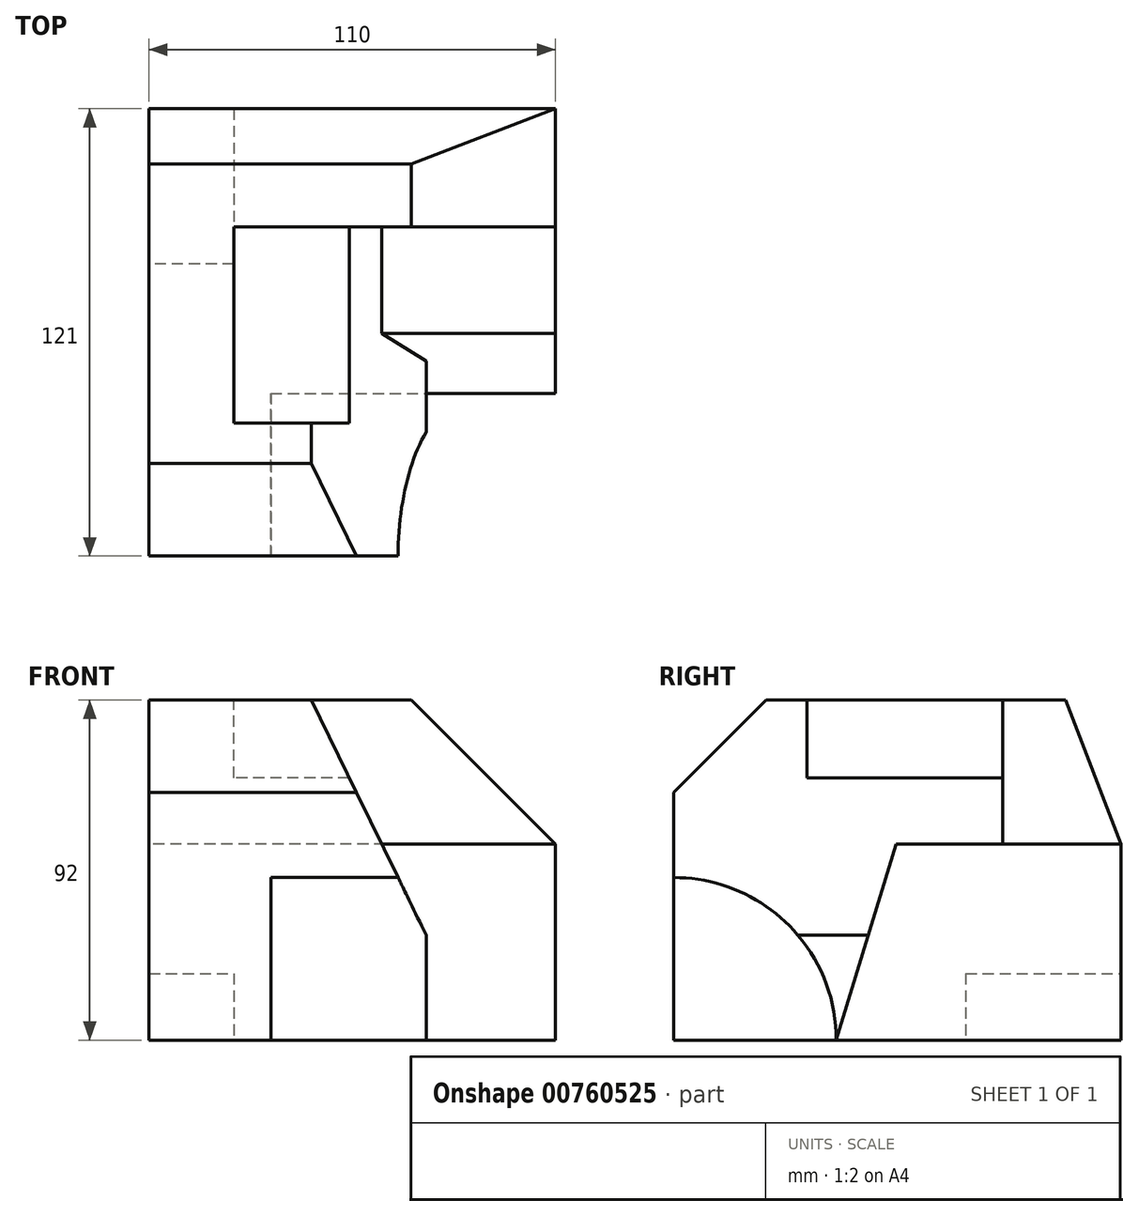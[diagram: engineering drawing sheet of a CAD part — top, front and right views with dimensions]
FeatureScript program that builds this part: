
annotation { "Feature Type Name" : "Feature", "Feature Type Description" : "" }
export const myFeature = defineFeature(function(context is Context, id is Id, definition is map)
    precondition{}
    {
        {
            var Q0;
            Q0=qCreatedBy(makeId("Front.planeOp"),FACE);
            var sketch = newSketch(context, id + "F0", { "sketchPlane" : qUnion([Q0])});
            skLineSegment(sketch, "E0", {"start": v(0, 0) * mm, "end": v(0, 92) * mm});
            skLineSegment(sketch, "E1", {"start": v(0, 92) * mm, "end": v(44, 92) * mm});
            skLineSegment(sketch, "E2", {"start": v(44, 92) * mm, "end": v(75, 28.44) * mm});
            skLineSegment(sketch, "E3", {"start": v(75, 28.44) * mm, "end": v(75, 0) * mm});
            skLineSegment(sketch, "E4", {"start": v(75, 0) * mm, "end": v(0, 0) * mm});
            skLineSegment(sketch, "E5", {"start": v(44, 92) * mm, "end": v(113.49, 92) * mm});
            skLineSegment(sketch, "E6", {"start": v(113.49, 92) * mm, "end": v(113.49, 53) * mm});
            skLineSegment(sketch, "E7", {"start": v(113.49, 53) * mm, "end": v(63.02, 53) * mm});
            skSolve(sketch);
        }
        {
            var Q0;
            Q0=qCreatedBy(makeId("Top.planeOp"),FACE);
            var sketch = newSketch(context, id + "F1", { "sketchPlane" : qUnion([Q0])});
            skLineSegment(sketch, "E8", {"start": v(0, 0) * mm, "end": v(0, 121) * mm});
            skLineSegment(sketch, "E9", {"start": v(0, 121) * mm, "end": v(110, 121) * mm});
            skLineSegment(sketch, "E10", {"start": v(110, 121) * mm, "end": v(110, 0) * mm});
            skLineSegment(sketch, "E11", {"start": v(110, 0) * mm, "end": v(0, 0) * mm});
            skLineSegment(sketch, "E12", {"start": v(0, 121) * mm, "end": v(23, 121) * mm});
            skLineSegment(sketch, "E13", {"start": v(23, 121) * mm, "end": v(23, 79) * mm});
            skLineSegment(sketch, "E14", {"start": v(23, 79) * mm, "end": v(0, 79) * mm});
            skLineSegment(sketch, "E15", {"start": v(0, 79) * mm, "end": v(0, 121) * mm});
            skSolve(sketch);
        }
        {
            var Q0;
            Q0=qCreatedBy(makeId("Right.planeOp"),FACE);
            var sketch = newSketch(context, id + "F2", { "sketchPlane" : qUnion([Q0])});
            skLineSegment(sketch, "E16", {"start": v(0, 0) * mm, "end": v(0, 67) * mm});
            skLineSegment(sketch, "E17", {"start": v(0, 67) * mm, "end": v(25, 92) * mm});
            skLineSegment(sketch, "E18", {"start": v(25, 92) * mm, "end": v(106.03, 92) * mm});
            skLineSegment(sketch, "E19", {"start": v(106.03, 92) * mm, "end": v(121, 53) * mm});
            skLineSegment(sketch, "E20", {"start": v(121, 53) * mm, "end": v(121, 0) * mm});
            skLineSegment(sketch, "E21", {"start": v(121, 0) * mm, "end": v(0, 0) * mm});
            skSolve(sketch);
        }
        {
            var Q0;
            Q0=makeQuery(id+"F0.imprint","IMPRINT",FACE,{"disambiguationData":[TD([[makeQuery(id+"F0.imprint","IMPRINT",EDGE,{"derivedFrom":sQuery(id+"F0.wireOp",EDGE,"E0")}),-1.0]])]});
            extrude(context, id + "F3", {"entities" : qUnion([Q0]), "oppositeDirection" : true, "depth" : 172 * mm, "offsetDistance" : 25 * mm});
        }
        {
            var Q0;
            Q0=makeQuery(id+"F2.imprint","IMPRINT",FACE,{"disambiguationData":[TD([[makeQuery(id+"F2.imprint","IMPRINT",EDGE,{"derivedFrom":sQuery(id+"F2.wireOp",EDGE,"E16")}),-1.0]])]});
            extrude(context, id + "F4", {"entities" : qUnion([Q0]), "operationType" : NewBodyOperationType.INTERSECT, "depth" : 150 * mm, "offsetDistance" : 25 * mm});
        }
        {
            var Q0;
            Q0=qCreatedBy(makeId("Front.planeOp"),FACE);
            cPlane(context, id + "F5", {"entities" : qUnion([Q0]), "cplaneType" : CPlaneType.OFFSET, "offset" : 44 * mm, "oppositeDirection" : true, "width" : 150 * mm, "height" : 150 * mm});
        }
        {
            var Q0;
            Q0=qCreatedBy(id+"F5.planeOp",FACE);
            var sketch = newSketch(context, id + "F6", { "sketchPlane" : qUnion([Q0])});
            skLineSegment(sketch, "E22", {"start": v(0, 0) * mm, "end": v(0, 92) * mm});
            skLineSegment(sketch, "E23", {"start": v(0, 92) * mm, "end": v(71, 92) * mm});
            skLineSegment(sketch, "E24", {"start": v(71, 92) * mm, "end": v(110, 53) * mm});
            skLineSegment(sketch, "E25", {"start": v(110, 53) * mm, "end": v(110, 0) * mm});
            skLineSegment(sketch, "E26", {"start": v(110, 0) * mm, "end": v(0, 0) * mm});
            skSolve(sketch);
        }
        {
            var Q0;
            Q0=makeQuery(id+"F6.imprint","IMPRINT",FACE,{"disambiguationData":[TD([[makeQuery(id+"F6.imprint","IMPRINT",EDGE,{"derivedFrom":sQuery(id+"F6.wireOp",EDGE,"E22")}),-1.0]])]});
            extrude(context, id + "F7", {"entities" : qUnion([Q0]), "oppositeDirection" : true, "depth" : 111 * mm, "offsetDistance" : 25 * mm});
        }
        {
            var Q0;
            Q0=makeQuery(id+"F2.imprint","IMPRINT",FACE,{"disambiguationData":[TD([[makeQuery(id+"F2.imprint","IMPRINT",EDGE,{"derivedFrom":sQuery(id+"F2.wireOp",EDGE,"E16")}),-1.0]])]});
            extrude(context, id + "F8", {"entities" : qUnion([Q0]), "operationType" : NewBodyOperationType.INTERSECT, "depth" : 163 * mm, "offsetDistance" : 25 * mm});
        }
        {
            var Q0;
            Q0=makeQuery(id+"F3.opExtrude","SWEPT_FACE",FACE,{"disambiguationData":[OSD([sQuery(id+"F0.wireOp",EDGE,"E3")])]});
            var sketch = newSketch(context, id + "F9", { "sketchPlane" : qUnion([Q0])});
            skCircle(sketch, "E27", {"center": v(0, 0) * mm, "radius": 44 * mm});
            skSolve(sketch);
        }
        {
            var Q0;
            {var subQ1=sQuery(id+"F0.wireOp",EDGE,"E3");var subQ6=makeQuery(id+"F3.opExtrude","CAP_EDGE",EDGE,{"disambiguationData":[OSD([subQ1])],"isStart":true});Q0=makeQuery(id+"F9.imprint","IMPRINT",FACE,{"disambiguationData":[TD([[makeQuery(id+"F9.imprint","IMPRINT",EDGE,{"derivedFrom":subQ6}),1.0]])]});}
            var Q1;
            {var subQ1=sQuery(id+"F0.wireOp",EDGE,"E3");var subQ6=makeQuery(id+"F3.opExtrude","CAP_EDGE",EDGE,{"disambiguationData":[OSD([subQ1])],"isStart":true});Q1=makeQuery(id+"F9.imprint","IMPRINT",FACE,{"disambiguationData":[TD([[makeQuery(id+"F9.imprint","IMPRINT",EDGE,{"derivedFrom":subQ6}),-1.0]])]});}
            extrude(context, id + "F10", {"entities" : qUnion([Q0, Q1]), "operationType" : NewBodyOperationType.REMOVE, "oppositeDirection" : true, "depth" : 42 * mm, "offsetDistance" : 25 * mm});
        }
        {
            var Q0;
            {var subQ0=sQuery(id+"F0.wireOp",EDGE,"E5");Q0=makeQuery(id+"F0.imprint","IMPRINT",FACE,{"disambiguationData":[TD([[makeQuery(id+"F0.imprint","IMPRINT",EDGE,{"derivedFrom":subQ0}),-1.0]])]});}
            extrude(context, id + "F11", {"entities" : qUnion([Q0]), "oppositeDirection" : true, "depth" : 89 * mm, "offsetDistance" : 25 * mm});
        }
        {
            var Q0;
            Q0=makeQuery(id+"F11.opExtrude","SWEPT_BODY",BODY,{"disambiguationData":[OSD([sQuery(id+"F0.wireOp",EDGE,"E2"),sQuery(id+"F0.wireOp",EDGE,"E5"),sQuery(id+"F0.wireOp",EDGE,"E6"),sQuery(id+"F0.wireOp",EDGE,"E7")])]});
            var Q1;
            Q1=makeQuery(id+"F7.opExtrude","SWEPT_BODY",BODY,{"disambiguationData":[OSD([sQuery(id+"F6.wireOp",EDGE,"E22"),sQuery(id+"F6.wireOp",EDGE,"E23"),sQuery(id+"F6.wireOp",EDGE,"E24"),sQuery(id+"F6.wireOp",EDGE,"E25"),sQuery(id+"F6.wireOp",EDGE,"E26")])]});
            booleanBodies(context, id + "F12", {"operationType" : BooleanOperationType.SUBTRACTION, "tools" : qUnion([Q0]), "targets" : qUnion([Q1])});
        }
        {
            var Q0;
            Q0=makeQuery(id+"F7.opExtrude","SWEPT_FACE",FACE,{"disambiguationData":[OSD([sQuery(id+"F6.wireOp",EDGE,"E25")])]});
            var sketch = newSketch(context, id + "F13", { "sketchPlane" : qUnion([Q0])});
            skLineSegment(sketch, "E28", {"start": v(44, 0) * mm, "end": v(60.2, 53) * mm});
            skLineSegment(sketch, "E29", {"start": v(60.2, 53) * mm, "end": v(44, 53) * mm});
            skLineSegment(sketch, "E30", {"start": v(44, 53) * mm, "end": v(44, 0) * mm});
            skSolve(sketch);
        }
        {
            var Q0;
            Q0=makeQuery(id+"F13.imprint","IMPRINT",FACE,{"disambiguationData":[TD([[makeQuery(id+"F13.imprint","IMPRINT",EDGE,{"derivedFrom":sQuery(id+"F13.wireOp",EDGE,"E28")}),1.0]])]});
            extrude(context, id + "F14", {"entities" : qUnion([Q0]), "oppositeDirection" : true, "depth" : 110 * mm, "offsetDistance" : 25 * mm});
        }
        {
            var Q0;
            Q0=makeQuery(id+"F14.opExtrude","SWEPT_BODY",BODY,{"disambiguationData":[OSD([sQuery(id+"F13.wireOp",EDGE,"E28"),sQuery(id+"F13.wireOp",EDGE,"E29"),sQuery(id+"F13.wireOp",EDGE,"E30")])]});
            var Q1;
            Q1=makeQuery(id+"F7.opExtrude","SWEPT_BODY",BODY,{"disambiguationData":[OSD([sQuery(id+"F6.wireOp",EDGE,"E22"),sQuery(id+"F6.wireOp",EDGE,"E23"),sQuery(id+"F6.wireOp",EDGE,"E24"),sQuery(id+"F6.wireOp",EDGE,"E25"),sQuery(id+"F6.wireOp",EDGE,"E26")])]});
            booleanBodies(context, id + "F15", {"operationType" : BooleanOperationType.SUBTRACTION, "tools" : qUnion([Q0]), "targets" : qUnion([Q1])});
        }
        {
            var Q0;
            Q0=makeQuery(id+"F3.opExtrude","SWEPT_BODY",BODY,{"disambiguationData":[OSD([sQuery(id+"F0.wireOp",EDGE,"E0"),sQuery(id+"F0.wireOp",EDGE,"E1"),sQuery(id+"F0.wireOp",EDGE,"E2"),sQuery(id+"F0.wireOp",EDGE,"E3"),sQuery(id+"F0.wireOp",EDGE,"E4")])]});
            var Q1;
            Q1=makeQuery(id+"F7.opExtrude","SWEPT_BODY",BODY,{"disambiguationData":[OSD([sQuery(id+"F6.wireOp",EDGE,"E22"),sQuery(id+"F6.wireOp",EDGE,"E23"),sQuery(id+"F6.wireOp",EDGE,"E24"),sQuery(id+"F6.wireOp",EDGE,"E25"),sQuery(id+"F6.wireOp",EDGE,"E26")])]});
            booleanBodies(context, id + "F16", {"operationType" : BooleanOperationType.UNION, "tools" : qUnion([Q0, Q1])});
        }
        {
            var Q0;
            Q0=makeQuery(id+"F16.opBoolean","MERGE",FACE,{"derivedFrom":[makeQuery(id+"F3.opExtrude","SWEPT_FACE",FACE,{"disambiguationData":[OSD([sQuery(id+"F0.wireOp",EDGE,"E1")])]}),makeQuery(id+"F7.opExtrude","SWEPT_FACE",FACE,{"disambiguationData":[OSD([sQuery(id+"F6.wireOp",EDGE,"E23")])]})]});
            var sketch = newSketch(context, id + "F17", { "sketchPlane" : qUnion([Q0])});
            skLineSegment(sketch, "E31", {"start": v(0, 121) * mm, "end": v(23, 121) * mm});
            skLineSegment(sketch, "E32", {"start": v(23, 121) * mm, "end": v(23, 36) * mm});
            skLineSegment(sketch, "E33", {"start": v(23, 36) * mm, "end": v(84.38, 36) * mm});
            skLineSegment(sketch, "E34", {"start": v(84.38, 36) * mm, "end": v(84.38, 89) * mm});
            skLineSegment(sketch, "E35", {"start": v(84.38, 89) * mm, "end": v(23, 89) * mm});
            skSolve(sketch);
        }
        {
            var Q0;
            {var subQ0=sQuery(id+"F17.wireOp",EDGE,"E33");var subQ1=sQuery(id+"F17.wireOp",EDGE,"E32");var subQ2=makeQuery(id+"F17.imprint","INTERSECT",VERTEX,{"derivedFrom":[subQ1,subQ0]});Q0=makeQuery(id+"F17.imprint","IMPRINT",FACE,{"disambiguationData":[TD([[makeQuery(id+"F17.imprint","IMPRINT",EDGE,{"disambiguationData":[TD([[subQ2,1.0]])],"derivedFrom":subQ1}),1.0]])]});}
            var Q1;
            {var subQ4=sQuery(id+"F17.wireOp",EDGE,"E34");Q1=makeQuery(id+"F17.imprint","IMPRINT",FACE,{"disambiguationData":[TD([[makeQuery(id+"F17.imprint","IMPRINT",EDGE,{"derivedFrom":subQ4}),1.0]])]});}
            extrude(context, id + "F18", {"entities" : qUnion([Q0, Q1]), "operationType" : NewBodyOperationType.REMOVE, "oppositeDirection" : true, "depth" : 21 * mm, "offsetDistance" : 25 * mm});
        }
        {
            var Q0;
            {var subQ4=sQuery(id+"F1.wireOp",EDGE,"E13");Q0=makeQuery(id+"F1.imprint","IMPRINT",FACE,{"disambiguationData":[TD([[makeQuery(id+"F1.imprint","IMPRINT",EDGE,{"derivedFrom":subQ4}),-1.0]])]});}
            extrude(context, id + "F19", {"entities" : qUnion([Q0]), "operationType" : NewBodyOperationType.REMOVE, "depth" : 18 * mm, "offsetDistance" : 25 * mm});
        }
    });
